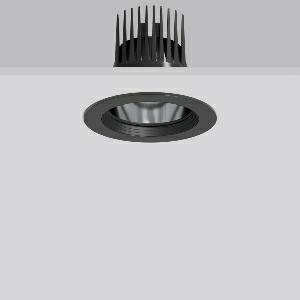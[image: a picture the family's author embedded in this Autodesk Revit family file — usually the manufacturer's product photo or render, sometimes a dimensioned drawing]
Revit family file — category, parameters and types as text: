
# Revit family: heledon_maxi_e_901763_003_2_be69
name_source: partatom
category: Lighting Fixtures
units: mm (PartAtom-declared; Revit-internal decimal feet)

## family parameters
Cut with Voids When Loaded = No
Host = Face
Light Source = No
Part Type = Normal
Room Calculation Point = No
Round Connector Dimension = Use Diameter
Shared = No

## types (1)
- HELEDON maxi E (1 x LED Modul 927, 4000 lm, 2700)
    Apparent Load = 35 VA
    Approval mark = CE
    CIE Flux Codes = 100 100 100 100 100
    Color Rendering = 92
    Color Temperature = 2700
    Default Elevation = 1800 mm
    Description = Series: HELEDON maxi
Round recessed downlight. Housing: die-cast aluminium, powder-coated. Black plastic ring and recessed LED to prevent glare from the side. Optical assembly with reflector made of MIRO-Silver with 98% total light reflection for outstanding efficiency - can be changed without tools. Best colour rendering index Ra>90. Suitable for Recessed ceiling mounting. Installation without tools thanks to spring fastening system. Including separate LED converter with connecting cable 600 mm.High quality converter without flickering and stroboscopic effect. Through-wiring box (5 pole) available as accessory. The following accessories can be mounted without use of tools: interchangeable lenses, decorative glasses, honeycomb louvre, clear and frosted diffusers, white interchangeable plastic ring. 
Colour: deep black, matt (RAL 9005)
Diameter: 162 mm
Height: 3 mm
Cut-out diameter: 152 mm
Recess height: 200 mm
Luminaire: recess height: 135 mm
Lamp: LED
Socket: without socket
Colour temperature: 2700K
Colour rendering index (CRI): 92
System power: 35 W
Rated luminous flux: 4000 lm
Luminous efficiency: 114 lm/W
Control gear: Regulated power supply
Protection class: II
Type of protection: IP 20
    Height = 0 mm  [stored 0 ft]
    Lamp = 1 x LED Modul 927
    Lamp Light Flux = 4000 lm
    Lamp count = 1
    Length = 162 mm
    Lifetime = 50000 h
    Luminous efficacy = 114 lm/W
    Manufacturer = RZB
    ModVariant = No
    Model = 901763.003.2
    Mounting Place = Ceiling
    Mounting Type = Recessed
    Number of Poles = 1
    OnlyDefault = Yes
    Power Factor = 1
    Product Name = HELEDON maxi E
    Product group = Recessed downlights
    ProductGroupID = 402
    Protection Class = Protection class II
    Protection Degree = IP 20
    RLX_Detail_Level = 1
    RLX_Emergency_Light_Flux = 0 lm
    RLX_Emergency_Type = 0
    RLX_Emergency_Type_DB = No
    RlxData = <blob elided: 121849 chars, md5=8e20bf81>
    Socket = socket
    Standby Power = 0 W
    System Light Flux = 4000 lm
    System Power = 35 W
    Type Comments = Product without accessories
    Type Image = 901662.003.jpg
    URL = http://relux.com
    VarID = ---
    Voltage = 230 V
    Voltage Range = 220-240 V
    Weight = 0.00 kg
    Width = 0 mm  [stored 0 ft]

note: [stored X ft] marks values corroborated as IEEE doubles in the binary element streams (Revit-internal decimal feet)

## geometry (parser evidence)
native form markers: Blend x4, Sweep x12
no freeform markers — native parametric forms only
